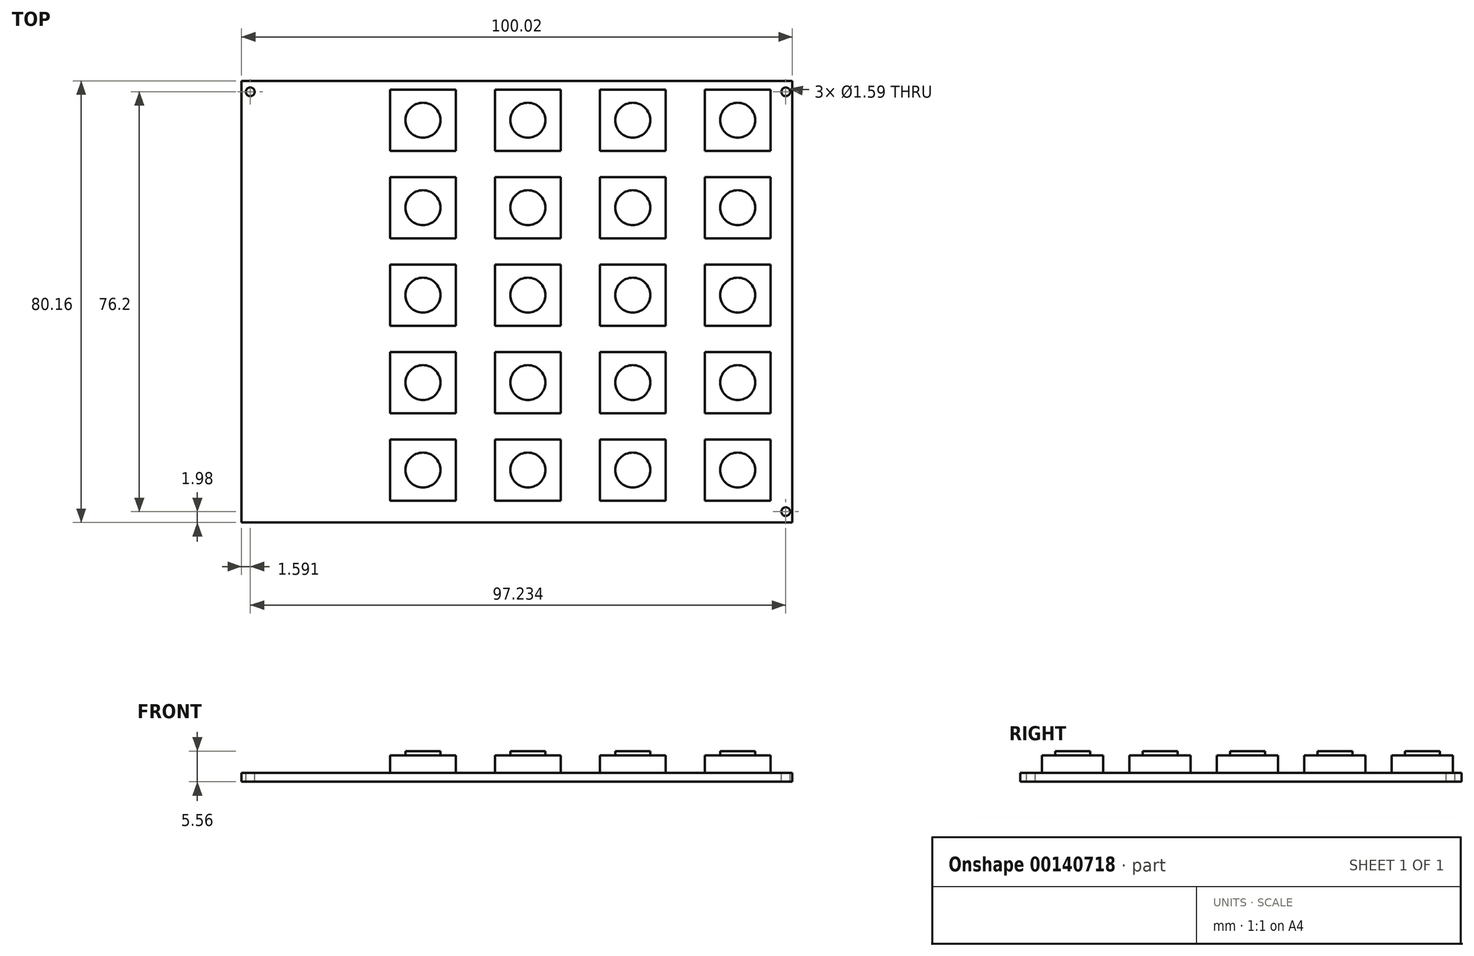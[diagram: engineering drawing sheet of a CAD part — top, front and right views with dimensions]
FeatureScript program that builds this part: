
annotation { "Feature Type Name" : "Feature", "Feature Type Description" : "" }
export const myFeature = defineFeature(function(context is Context, id is Id, definition is map)
    precondition{}
    {
        {
            var Q0;
            Q0=qCreatedBy(makeId("Top.planeOp"),FACE);
            var sketch = newSketch(context, id + "F0", { "sketchPlane" : qUnion([Q0])});
            skLineSegment(sketch, "E0.bottom", {"start": v(50, -40.08) * mm, "end": v(-50, -40.08) * mm});
            skLineSegment(sketch, "E0.top", {"start": v(50, 40.08) * mm, "end": v(-50, 40.08) * mm});
            skLineSegment(sketch, "E0.left", {"start": v(50, -40.08) * mm, "end": v(50, 40.08) * mm});
            skLineSegment(sketch, "E0.right", {"start": v(-50, -40.08) * mm, "end": v(-50, 40.08) * mm});
            skPoint(sketch, "E0.middle", {"position": v(0, 0) * mm});
            skSolve(sketch);
        }
        {
            var Q0;
            Q0 = qSketchRegion(id + "F0", true);
            extrude(context, id + "F1", {"entities" : qUnion([Q0]), "depth" : 1.59 * mm});
        }
        {
            var Q0;
            Q0=makeQuery(id+"F1.opExtrude","CAP_FACE",FACE,{"disambiguationData":[OSD([sQuery(id+"F0.wireOp",EDGE,"E0.bottom"),sQuery(id+"F0.wireOp",EDGE,"E0.top"),sQuery(id+"F0.wireOp",EDGE,"E0.left"),sQuery(id+"F0.wireOp",EDGE,"E0.right")])],"isStart":false});
            var sketch = newSketch(context, id + "F2", { "sketchPlane" : qUnion([Q0])});
            skLineSegment(sketch, "E1.0.0", {"start": v(-50, -40.08) * mm, "end": v(50, -40.08) * mm});
            skLineSegment(sketch, "E1.0.1", {"start": v(50, -40.08) * mm, "end": v(50, 40.08) * mm});
            skLineSegment(sketch, "E1.0.2", {"start": v(50, 40.08) * mm, "end": v(-50, 40.08) * mm});
            skLineSegment(sketch, "E1.0.3", {"start": v(-50, 40.08) * mm, "end": v(-50, -40.08) * mm});
            skLineSegment(sketch, "E2.bottom", {"start": v(50, -40.08) * mm, "end": v(46.04, -40.08) * mm});
            skLineSegment(sketch, "E2.top", {"start": v(50, -36.12) * mm, "end": v(46.04, -36.12) * mm});
            skLineSegment(sketch, "E2.left", {"start": v(50, -40.08) * mm, "end": v(50, -36.12) * mm});
            skLineSegment(sketch, "E2.right", {"start": v(46.04, -40.08) * mm, "end": v(46.04, -36.12) * mm});
            skLineSegment(sketch, "E3.bottom", {"start": v(46.04, -36.12) * mm, "end": v(34.13, -36.12) * mm});
            skLineSegment(sketch, "E3.top", {"start": v(46.04, -25) * mm, "end": v(34.13, -25) * mm});
            skLineSegment(sketch, "E3.left", {"start": v(46.04, -36.12) * mm, "end": v(46.04, -25) * mm});
            skLineSegment(sketch, "E3.right", {"start": v(34.13, -36.12) * mm, "end": v(34.13, -25) * mm});
            skLineSegment(sketch, "E4", {"start": v(40.08, 40.08) * mm, "end": v(40.08, 38.5) * mm});
            skLineSegment(sketch, "E5", {"start": v(-50, -30.15) * mm, "end": v(-23.02, -30.15) * mm});
            skLineSegment(sketch, "E6.0.1.0", {"start": v(46.04, -9.13) * mm, "end": v(34.13, -9.13) * mm});
            skLineSegment(sketch, "E6.0.1.1", {"start": v(34.13, -20.24) * mm, "end": v(34.13, -9.13) * mm});
            skLineSegment(sketch, "E6.0.1.2", {"start": v(46.04, -20.24) * mm, "end": v(34.13, -20.24) * mm});
            skLineSegment(sketch, "E6.0.1.3", {"start": v(46.04, -20.24) * mm, "end": v(46.04, -9.13) * mm});
            skLineSegment(sketch, "E6.0.2.0", {"start": v(46.04, 6.75) * mm, "end": v(34.13, 6.75) * mm});
            skLineSegment(sketch, "E6.0.2.1", {"start": v(34.13, -4.37) * mm, "end": v(34.13, 6.75) * mm});
            skLineSegment(sketch, "E6.0.2.2", {"start": v(46.04, -4.37) * mm, "end": v(34.13, -4.37) * mm});
            skLineSegment(sketch, "E6.0.2.3", {"start": v(46.04, -4.37) * mm, "end": v(46.04, 6.75) * mm});
            skLineSegment(sketch, "E6.0.3.0", {"start": v(46.04, 22.62) * mm, "end": v(34.13, 22.62) * mm});
            skLineSegment(sketch, "E6.0.3.1", {"start": v(34.13, 11.5) * mm, "end": v(34.13, 22.62) * mm});
            skLineSegment(sketch, "E6.0.3.2", {"start": v(46.04, 11.5) * mm, "end": v(34.13, 11.5) * mm});
            skLineSegment(sketch, "E6.0.3.3", {"start": v(46.04, 11.5) * mm, "end": v(46.04, 22.62) * mm});
            skLineSegment(sketch, "E6.0.4.0", {"start": v(46.04, 38.5) * mm, "end": v(34.13, 38.5) * mm});
            skLineSegment(sketch, "E6.0.4.1", {"start": v(34.13, 27.38) * mm, "end": v(34.13, 38.5) * mm});
            skLineSegment(sketch, "E6.0.4.2", {"start": v(46.04, 27.38) * mm, "end": v(34.13, 27.38) * mm});
            skLineSegment(sketch, "E6.0.4.3", {"start": v(46.04, 27.38) * mm, "end": v(46.04, 38.5) * mm});
            skLineSegment(sketch, "E6.1.0.0", {"start": v(26.99, -25) * mm, "end": v(15.08, -25) * mm});
            skLineSegment(sketch, "E6.1.0.1", {"start": v(15.08, -36.12) * mm, "end": v(15.08, -25) * mm});
            skLineSegment(sketch, "E6.1.0.2", {"start": v(26.99, -36.12) * mm, "end": v(15.08, -36.12) * mm});
            skLineSegment(sketch, "E6.1.0.3", {"start": v(26.99, -36.12) * mm, "end": v(26.99, -25) * mm});
            skLineSegment(sketch, "E6.1.1.0", {"start": v(26.99, -9.13) * mm, "end": v(15.08, -9.13) * mm});
            skLineSegment(sketch, "E6.1.1.1", {"start": v(15.08, -20.24) * mm, "end": v(15.08, -9.13) * mm});
            skLineSegment(sketch, "E6.1.1.2", {"start": v(26.99, -20.24) * mm, "end": v(15.08, -20.24) * mm});
            skLineSegment(sketch, "E6.1.1.3", {"start": v(26.99, -20.24) * mm, "end": v(26.99, -9.13) * mm});
            skLineSegment(sketch, "E6.1.2.0", {"start": v(26.99, 6.75) * mm, "end": v(15.08, 6.75) * mm});
            skLineSegment(sketch, "E6.1.2.1", {"start": v(15.08, -4.37) * mm, "end": v(15.08, 6.75) * mm});
            skLineSegment(sketch, "E6.1.2.2", {"start": v(26.99, -4.37) * mm, "end": v(15.08, -4.37) * mm});
            skLineSegment(sketch, "E6.1.2.3", {"start": v(26.99, -4.37) * mm, "end": v(26.99, 6.75) * mm});
            skLineSegment(sketch, "E6.1.3.0", {"start": v(26.99, 22.62) * mm, "end": v(15.08, 22.62) * mm});
            skLineSegment(sketch, "E6.1.3.1", {"start": v(15.08, 11.5) * mm, "end": v(15.08, 22.62) * mm});
            skLineSegment(sketch, "E6.1.3.2", {"start": v(26.99, 11.5) * mm, "end": v(15.08, 11.5) * mm});
            skLineSegment(sketch, "E6.1.3.3", {"start": v(26.99, 11.5) * mm, "end": v(26.99, 22.62) * mm});
            skLineSegment(sketch, "E6.1.4.0", {"start": v(26.99, 38.5) * mm, "end": v(15.08, 38.5) * mm});
            skLineSegment(sketch, "E6.1.4.1", {"start": v(15.08, 27.38) * mm, "end": v(15.08, 38.5) * mm});
            skLineSegment(sketch, "E6.1.4.2", {"start": v(26.99, 27.38) * mm, "end": v(15.08, 27.38) * mm});
            skLineSegment(sketch, "E6.1.4.3", {"start": v(26.99, 27.38) * mm, "end": v(26.99, 38.5) * mm});
            skLineSegment(sketch, "E6.2.0.0", {"start": v(7.94, -25) * mm, "end": v(-3.97, -25) * mm});
            skLineSegment(sketch, "E6.2.0.1", {"start": v(-3.97, -36.12) * mm, "end": v(-3.97, -25) * mm});
            skLineSegment(sketch, "E6.2.0.2", {"start": v(7.94, -36.12) * mm, "end": v(-3.97, -36.12) * mm});
            skLineSegment(sketch, "E6.2.0.3", {"start": v(7.94, -36.12) * mm, "end": v(7.94, -25) * mm});
            skLineSegment(sketch, "E6.2.1.0", {"start": v(7.94, -9.13) * mm, "end": v(-3.97, -9.13) * mm});
            skLineSegment(sketch, "E6.2.1.1", {"start": v(-3.97, -20.24) * mm, "end": v(-3.97, -9.13) * mm});
            skLineSegment(sketch, "E6.2.1.2", {"start": v(7.94, -20.24) * mm, "end": v(-3.97, -20.24) * mm});
            skLineSegment(sketch, "E6.2.1.3", {"start": v(7.94, -20.24) * mm, "end": v(7.94, -9.13) * mm});
            skLineSegment(sketch, "E6.2.2.0", {"start": v(7.94, 6.75) * mm, "end": v(-3.97, 6.75) * mm});
            skLineSegment(sketch, "E6.2.2.1", {"start": v(-3.97, -4.37) * mm, "end": v(-3.97, 6.75) * mm});
            skLineSegment(sketch, "E6.2.2.2", {"start": v(7.94, -4.37) * mm, "end": v(-3.97, -4.37) * mm});
            skLineSegment(sketch, "E6.2.2.3", {"start": v(7.94, -4.37) * mm, "end": v(7.94, 6.75) * mm});
            skLineSegment(sketch, "E6.2.3.0", {"start": v(7.94, 22.62) * mm, "end": v(-3.97, 22.62) * mm});
            skLineSegment(sketch, "E6.2.3.1", {"start": v(-3.97, 11.5) * mm, "end": v(-3.97, 22.62) * mm});
            skLineSegment(sketch, "E6.2.3.2", {"start": v(7.94, 11.5) * mm, "end": v(-3.97, 11.5) * mm});
            skLineSegment(sketch, "E6.2.3.3", {"start": v(7.94, 11.5) * mm, "end": v(7.94, 22.62) * mm});
            skLineSegment(sketch, "E6.2.4.0", {"start": v(7.94, 38.5) * mm, "end": v(-3.97, 38.5) * mm});
            skLineSegment(sketch, "E6.2.4.1", {"start": v(-3.97, 27.38) * mm, "end": v(-3.97, 38.5) * mm});
            skLineSegment(sketch, "E6.2.4.2", {"start": v(7.94, 27.38) * mm, "end": v(-3.97, 27.38) * mm});
            skLineSegment(sketch, "E6.2.4.3", {"start": v(7.94, 27.38) * mm, "end": v(7.94, 38.5) * mm});
            skLineSegment(sketch, "E6.3.0.0", {"start": v(-11.11, -25) * mm, "end": v(-23.02, -25) * mm});
            skLineSegment(sketch, "E6.3.0.1", {"start": v(-23.02, -36.12) * mm, "end": v(-23.02, -25) * mm});
            skLineSegment(sketch, "E6.3.0.2", {"start": v(-11.11, -36.12) * mm, "end": v(-23.02, -36.12) * mm});
            skLineSegment(sketch, "E6.3.0.3", {"start": v(-11.11, -36.12) * mm, "end": v(-11.11, -25) * mm});
            skLineSegment(sketch, "E6.3.1.0", {"start": v(-11.11, -9.13) * mm, "end": v(-23.02, -9.13) * mm});
            skLineSegment(sketch, "E6.3.1.1", {"start": v(-23.02, -20.24) * mm, "end": v(-23.02, -9.13) * mm});
            skLineSegment(sketch, "E6.3.1.2", {"start": v(-11.11, -20.24) * mm, "end": v(-23.02, -20.24) * mm});
            skLineSegment(sketch, "E6.3.1.3", {"start": v(-11.11, -20.24) * mm, "end": v(-11.11, -9.13) * mm});
            skLineSegment(sketch, "E6.3.2.0", {"start": v(-11.11, 6.75) * mm, "end": v(-23.02, 6.75) * mm});
            skLineSegment(sketch, "E6.3.2.1", {"start": v(-23.02, -4.37) * mm, "end": v(-23.02, 6.75) * mm});
            skLineSegment(sketch, "E6.3.2.2", {"start": v(-11.11, -4.37) * mm, "end": v(-23.02, -4.37) * mm});
            skLineSegment(sketch, "E6.3.2.3", {"start": v(-11.11, -4.37) * mm, "end": v(-11.11, 6.75) * mm});
            skLineSegment(sketch, "E6.3.3.0", {"start": v(-11.11, 22.62) * mm, "end": v(-23.02, 22.62) * mm});
            skLineSegment(sketch, "E6.3.3.1", {"start": v(-23.02, 11.5) * mm, "end": v(-23.02, 22.62) * mm});
            skLineSegment(sketch, "E6.3.3.2", {"start": v(-11.11, 11.5) * mm, "end": v(-23.02, 11.5) * mm});
            skLineSegment(sketch, "E6.3.3.3", {"start": v(-11.11, 11.5) * mm, "end": v(-11.11, 22.62) * mm});
            skLineSegment(sketch, "E6.3.4.0", {"start": v(-11.11, 38.5) * mm, "end": v(-23.02, 38.5) * mm});
            skLineSegment(sketch, "E6.3.4.1", {"start": v(-23.02, 27.38) * mm, "end": v(-23.02, 38.5) * mm});
            skLineSegment(sketch, "E6.3.4.2", {"start": v(-11.11, 27.38) * mm, "end": v(-23.02, 27.38) * mm});
            skLineSegment(sketch, "E6.3.4.3", {"start": v(-11.11, 27.38) * mm, "end": v(-11.11, 38.5) * mm});
            skLineSegment(sketch, "E6.direction1", {"start": v(34.13, -25) * mm, "end": v(15.08, -25) * mm, "construction": true});
            skLineSegment(sketch, "E6.direction2", {"start": v(34.13, -25) * mm, "end": v(34.13, -9.13) * mm, "construction": true});
            skSolve(sketch);
        }
        {
            var Q0;
            Q0=makeQuery(id+"F2.imprint","IMPRINT",FACE,{"disambiguationData":[TD([[makeQuery(id+"F2.imprint","IMPRINT",EDGE,{"derivedFrom":sQuery(id+"F2.wireOp",EDGE,"E6.3.4.0")}),1.0]])]});
            var Q1;
            Q1=makeQuery(id+"F2.imprint","IMPRINT",FACE,{"disambiguationData":[TD([[makeQuery(id+"F2.imprint","IMPRINT",EDGE,{"derivedFrom":sQuery(id+"F2.wireOp",EDGE,"E6.2.4.0")}),1.0]])]});
            var Q2;
            Q2=makeQuery(id+"F2.imprint","IMPRINT",FACE,{"disambiguationData":[TD([[makeQuery(id+"F2.imprint","IMPRINT",EDGE,{"derivedFrom":sQuery(id+"F2.wireOp",EDGE,"E6.1.4.0")}),1.0]])]});
            var Q3;
            {var subQ0=sQuery(id+"F2.wireOp",EDGE,"E6.0.4.1");Q3=makeQuery(id+"F2.imprint","IMPRINT",FACE,{"disambiguationData":[TD([[makeQuery(id+"F2.imprint","IMPRINT",EDGE,{"derivedFrom":subQ0}),-1.0]])]});}
            var Q4;
            Q4=makeQuery(id+"F2.imprint","IMPRINT",FACE,{"disambiguationData":[TD([[makeQuery(id+"F2.imprint","IMPRINT",EDGE,{"derivedFrom":sQuery(id+"F2.wireOp",EDGE,"E6.0.3.0")}),1.0]])]});
            var Q5;
            Q5=makeQuery(id+"F2.imprint","IMPRINT",FACE,{"disambiguationData":[TD([[makeQuery(id+"F2.imprint","IMPRINT",EDGE,{"derivedFrom":sQuery(id+"F2.wireOp",EDGE,"E6.0.2.0")}),1.0]])]});
            var Q6;
            Q6=makeQuery(id+"F2.imprint","IMPRINT",FACE,{"disambiguationData":[TD([[makeQuery(id+"F2.imprint","IMPRINT",EDGE,{"derivedFrom":sQuery(id+"F2.wireOp",EDGE,"E6.0.1.0")}),1.0]])]});
            var Q7;
            Q7=makeQuery(id+"F2.imprint","IMPRINT",FACE,{"disambiguationData":[TD([[makeQuery(id+"F2.imprint","IMPRINT",EDGE,{"derivedFrom":sQuery(id+"F2.wireOp",EDGE,"E3.bottom")}),-1.0]])]});
            var Q8;
            Q8=makeQuery(id+"F2.imprint","IMPRINT",FACE,{"disambiguationData":[TD([[makeQuery(id+"F2.imprint","IMPRINT",EDGE,{"derivedFrom":sQuery(id+"F2.wireOp",EDGE,"E6.1.0.0")}),1.0]])]});
            var Q9;
            Q9=makeQuery(id+"F2.imprint","IMPRINT",FACE,{"disambiguationData":[TD([[makeQuery(id+"F2.imprint","IMPRINT",EDGE,{"derivedFrom":sQuery(id+"F2.wireOp",EDGE,"E6.2.0.0")}),1.0]])]});
            var Q10;
            {var subQ3=sQuery(id+"F2.wireOp",EDGE,"E6.3.0.0");Q10=makeQuery(id+"F2.imprint","IMPRINT",FACE,{"disambiguationData":[TD([[makeQuery(id+"F2.imprint","IMPRINT",EDGE,{"derivedFrom":subQ3}),1.0]])]});}
            var Q11;
            Q11=makeQuery(id+"F2.imprint","IMPRINT",FACE,{"disambiguationData":[TD([[makeQuery(id+"F2.imprint","IMPRINT",EDGE,{"derivedFrom":sQuery(id+"F2.wireOp",EDGE,"E6.3.1.0")}),1.0]])]});
            var Q12;
            Q12=makeQuery(id+"F2.imprint","IMPRINT",FACE,{"disambiguationData":[TD([[makeQuery(id+"F2.imprint","IMPRINT",EDGE,{"derivedFrom":sQuery(id+"F2.wireOp",EDGE,"E6.3.2.0")}),1.0]])]});
            var Q13;
            Q13=makeQuery(id+"F2.imprint","IMPRINT",FACE,{"disambiguationData":[TD([[makeQuery(id+"F2.imprint","IMPRINT",EDGE,{"derivedFrom":sQuery(id+"F2.wireOp",EDGE,"E6.3.3.0")}),1.0]])]});
            var Q14;
            Q14=makeQuery(id+"F2.imprint","IMPRINT",FACE,{"disambiguationData":[TD([[makeQuery(id+"F2.imprint","IMPRINT",EDGE,{"derivedFrom":sQuery(id+"F2.wireOp",EDGE,"E6.2.3.0")}),1.0]])]});
            var Q15;
            Q15=makeQuery(id+"F2.imprint","IMPRINT",FACE,{"disambiguationData":[TD([[makeQuery(id+"F2.imprint","IMPRINT",EDGE,{"derivedFrom":sQuery(id+"F2.wireOp",EDGE,"E6.1.3.0")}),1.0]])]});
            var Q16;
            Q16=makeQuery(id+"F2.imprint","IMPRINT",FACE,{"disambiguationData":[TD([[makeQuery(id+"F2.imprint","IMPRINT",EDGE,{"derivedFrom":sQuery(id+"F2.wireOp",EDGE,"E6.1.2.0")}),1.0]])]});
            var Q17;
            Q17=makeQuery(id+"F2.imprint","IMPRINT",FACE,{"disambiguationData":[TD([[makeQuery(id+"F2.imprint","IMPRINT",EDGE,{"derivedFrom":sQuery(id+"F2.wireOp",EDGE,"E6.2.2.0")}),1.0]])]});
            var Q18;
            Q18=makeQuery(id+"F2.imprint","IMPRINT",FACE,{"disambiguationData":[TD([[makeQuery(id+"F2.imprint","IMPRINT",EDGE,{"derivedFrom":sQuery(id+"F2.wireOp",EDGE,"E6.2.1.0")}),1.0]])]});
            var Q19;
            Q19=makeQuery(id+"F2.imprint","IMPRINT",FACE,{"disambiguationData":[TD([[makeQuery(id+"F2.imprint","IMPRINT",EDGE,{"derivedFrom":sQuery(id+"F2.wireOp",EDGE,"E6.1.1.0")}),1.0]])]});
            extrude(context, id + "F3", {"entities" : qUnion([Q0, Q1, Q2, Q3, Q4, Q5, Q6, Q7, Q8, Q9, Q10, Q11, Q12, Q13, Q14, Q15, Q16, Q17, Q18, Q19]), "operationType" : NewBodyOperationType.ADD, "depth" : 3.17 * mm});
        }
        {
            var Q0;
            Q0=makeQuery(id+"F3.opExtrude","CAP_FACE",FACE,{"disambiguationData":[OSD([sQuery(id+"F2.wireOp",EDGE,"E6.2.3.0"),sQuery(id+"F2.wireOp",EDGE,"E6.2.3.1"),sQuery(id+"F2.wireOp",EDGE,"E6.2.3.2"),sQuery(id+"F2.wireOp",EDGE,"E6.2.3.3")])],"isStart":false});
            var sketch = newSketch(context, id + "F4", { "sketchPlane" : qUnion([Q0])});
            skLineSegment(sketch, "E7.0.0", {"start": v(-11.11, 27.38) * mm, "end": v(-11.11, 38.5) * mm});
            skLineSegment(sketch, "E7.0.1", {"start": v(-11.11, 38.5) * mm, "end": v(-23.02, 38.5) * mm});
            skLineSegment(sketch, "E7.0.2", {"start": v(-23.02, 38.5) * mm, "end": v(-23.02, 27.38) * mm});
            skLineSegment(sketch, "E7.0.3", {"start": v(-23.02, 27.38) * mm, "end": v(-11.11, 27.38) * mm});
            skLineSegment(sketch, "E8.0.0", {"start": v(7.94, 27.38) * mm, "end": v(7.94, 38.5) * mm});
            skLineSegment(sketch, "E8.0.1", {"start": v(7.94, 38.5) * mm, "end": v(-3.97, 38.5) * mm});
            skLineSegment(sketch, "E8.0.2", {"start": v(-3.97, 38.5) * mm, "end": v(-3.97, 27.38) * mm});
            skLineSegment(sketch, "E8.0.3", {"start": v(-3.97, 27.38) * mm, "end": v(7.94, 27.38) * mm});
            skLineSegment(sketch, "E9.0.0", {"start": v(26.99, 27.38) * mm, "end": v(26.99, 38.5) * mm});
            skLineSegment(sketch, "E9.0.1", {"start": v(26.99, 38.5) * mm, "end": v(15.08, 38.5) * mm});
            skLineSegment(sketch, "E9.0.2", {"start": v(15.08, 38.5) * mm, "end": v(15.08, 27.38) * mm});
            skLineSegment(sketch, "E9.0.3", {"start": v(15.08, 27.38) * mm, "end": v(26.99, 27.38) * mm});
            skLineSegment(sketch, "E10.0.0", {"start": v(46.04, 27.38) * mm, "end": v(46.04, 38.5) * mm});
            skLineSegment(sketch, "E10.0.1", {"start": v(46.04, 38.5) * mm, "end": v(34.13, 38.5) * mm});
            skLineSegment(sketch, "E10.0.2", {"start": v(34.13, 38.5) * mm, "end": v(34.13, 27.38) * mm});
            skLineSegment(sketch, "E10.0.3", {"start": v(34.13, 27.38) * mm, "end": v(46.04, 27.38) * mm});
            skLineSegment(sketch, "E11.0.0", {"start": v(46.04, 11.5) * mm, "end": v(46.04, 22.62) * mm});
            skLineSegment(sketch, "E11.0.1", {"start": v(46.04, 22.62) * mm, "end": v(34.13, 22.62) * mm});
            skLineSegment(sketch, "E11.0.2", {"start": v(34.13, 22.62) * mm, "end": v(34.13, 11.5) * mm});
            skLineSegment(sketch, "E11.0.3", {"start": v(34.13, 11.5) * mm, "end": v(46.04, 11.5) * mm});
            skLineSegment(sketch, "E12.0.0", {"start": v(46.04, -4.37) * mm, "end": v(46.04, 6.75) * mm});
            skLineSegment(sketch, "E12.0.1", {"start": v(46.04, 6.75) * mm, "end": v(34.13, 6.75) * mm});
            skLineSegment(sketch, "E12.0.2", {"start": v(34.13, 6.75) * mm, "end": v(34.13, -4.37) * mm});
            skLineSegment(sketch, "E12.0.3", {"start": v(34.13, -4.37) * mm, "end": v(46.04, -4.37) * mm});
            skLineSegment(sketch, "E13.0.0", {"start": v(46.04, -20.24) * mm, "end": v(46.04, -9.13) * mm});
            skLineSegment(sketch, "E13.0.1", {"start": v(46.04, -9.13) * mm, "end": v(34.13, -9.13) * mm});
            skLineSegment(sketch, "E13.0.2", {"start": v(34.13, -9.13) * mm, "end": v(34.13, -20.24) * mm});
            skLineSegment(sketch, "E13.0.3", {"start": v(34.13, -20.24) * mm, "end": v(46.04, -20.24) * mm});
            skLineSegment(sketch, "E14.0.0", {"start": v(34.13, -36.12) * mm, "end": v(46.04, -36.12) * mm});
            skLineSegment(sketch, "E14.0.1", {"start": v(46.04, -36.12) * mm, "end": v(46.04, -25) * mm});
            skLineSegment(sketch, "E14.0.2", {"start": v(46.04, -25) * mm, "end": v(34.13, -25) * mm});
            skLineSegment(sketch, "E14.0.3", {"start": v(34.13, -25) * mm, "end": v(34.13, -36.12) * mm});
            skLineSegment(sketch, "E15.0.0", {"start": v(26.99, -36.12) * mm, "end": v(26.99, -25) * mm});
            skLineSegment(sketch, "E15.0.1", {"start": v(26.99, -25) * mm, "end": v(15.08, -25) * mm});
            skLineSegment(sketch, "E15.0.2", {"start": v(15.08, -25) * mm, "end": v(15.08, -36.12) * mm});
            skLineSegment(sketch, "E15.0.3", {"start": v(15.08, -36.12) * mm, "end": v(26.99, -36.12) * mm});
            skLineSegment(sketch, "E16.0.0", {"start": v(7.94, -36.12) * mm, "end": v(7.94, -25) * mm});
            skLineSegment(sketch, "E16.0.1", {"start": v(7.94, -25) * mm, "end": v(-3.97, -25) * mm});
            skLineSegment(sketch, "E16.0.2", {"start": v(-3.97, -25) * mm, "end": v(-3.97, -36.12) * mm});
            skLineSegment(sketch, "E16.0.3", {"start": v(-3.97, -36.12) * mm, "end": v(7.94, -36.12) * mm});
            skLineSegment(sketch, "E17.0.0", {"start": v(-11.11, -36.12) * mm, "end": v(-11.11, -25) * mm});
            skLineSegment(sketch, "E17.0.1", {"start": v(-11.11, -25) * mm, "end": v(-23.02, -25) * mm});
            skLineSegment(sketch, "E17.0.2", {"start": v(-23.02, -25) * mm, "end": v(-23.02, -36.12) * mm});
            skLineSegment(sketch, "E17.0.3", {"start": v(-23.02, -36.12) * mm, "end": v(-11.11, -36.12) * mm});
            skLineSegment(sketch, "E18.0.0", {"start": v(-11.11, -20.24) * mm, "end": v(-11.11, -9.13) * mm});
            skLineSegment(sketch, "E18.0.1", {"start": v(-11.11, -9.13) * mm, "end": v(-23.02, -9.13) * mm});
            skLineSegment(sketch, "E18.0.2", {"start": v(-23.02, -9.13) * mm, "end": v(-23.02, -20.24) * mm});
            skLineSegment(sketch, "E18.0.3", {"start": v(-23.02, -20.24) * mm, "end": v(-11.11, -20.24) * mm});
            skLineSegment(sketch, "E19.0.0", {"start": v(-11.11, -4.37) * mm, "end": v(-11.11, 6.75) * mm});
            skLineSegment(sketch, "E19.0.1", {"start": v(-11.11, 6.75) * mm, "end": v(-23.02, 6.75) * mm});
            skLineSegment(sketch, "E19.0.2", {"start": v(-23.02, 6.75) * mm, "end": v(-23.02, -4.37) * mm});
            skLineSegment(sketch, "E19.0.3", {"start": v(-23.02, -4.37) * mm, "end": v(-11.11, -4.37) * mm});
            skLineSegment(sketch, "E20.0.0", {"start": v(-11.11, 11.5) * mm, "end": v(-11.11, 22.62) * mm});
            skLineSegment(sketch, "E20.0.1", {"start": v(-11.11, 22.62) * mm, "end": v(-23.02, 22.62) * mm});
            skLineSegment(sketch, "E20.0.2", {"start": v(-23.02, 22.62) * mm, "end": v(-23.02, 11.5) * mm});
            skLineSegment(sketch, "E20.0.3", {"start": v(-23.02, 11.5) * mm, "end": v(-11.11, 11.5) * mm});
            skLineSegment(sketch, "E21.0.0", {"start": v(7.94, 11.5) * mm, "end": v(7.94, 22.62) * mm});
            skLineSegment(sketch, "E21.0.1", {"start": v(7.94, 22.62) * mm, "end": v(-3.97, 22.62) * mm});
            skLineSegment(sketch, "E21.0.2", {"start": v(-3.97, 22.62) * mm, "end": v(-3.97, 11.5) * mm});
            skLineSegment(sketch, "E21.0.3", {"start": v(-3.97, 11.5) * mm, "end": v(7.94, 11.5) * mm});
            skLineSegment(sketch, "E22.0.0", {"start": v(7.94, -4.37) * mm, "end": v(7.94, 6.75) * mm});
            skLineSegment(sketch, "E22.0.1", {"start": v(7.94, 6.75) * mm, "end": v(-3.97, 6.75) * mm});
            skLineSegment(sketch, "E22.0.2", {"start": v(-3.97, 6.75) * mm, "end": v(-3.97, -4.37) * mm});
            skLineSegment(sketch, "E22.0.3", {"start": v(-3.97, -4.37) * mm, "end": v(7.94, -4.37) * mm});
            skLineSegment(sketch, "E23.0", {"start": v(7.94, -20.24) * mm, "end": v(-3.97, -20.24) * mm});
            skLineSegment(sketch, "E24.0.0", {"start": v(26.99, -20.24) * mm, "end": v(26.99, -9.13) * mm});
            skLineSegment(sketch, "E24.0.1", {"start": v(26.99, -9.13) * mm, "end": v(15.08, -9.13) * mm});
            skLineSegment(sketch, "E24.0.2", {"start": v(15.08, -9.13) * mm, "end": v(15.08, -20.24) * mm});
            skLineSegment(sketch, "E24.0.3", {"start": v(15.08, -20.24) * mm, "end": v(26.99, -20.24) * mm});
            skLineSegment(sketch, "E25.0.0", {"start": v(26.99, -4.37) * mm, "end": v(26.99, 6.75) * mm});
            skLineSegment(sketch, "E25.0.1", {"start": v(26.99, 6.75) * mm, "end": v(15.08, 6.75) * mm});
            skLineSegment(sketch, "E25.0.2", {"start": v(15.08, 6.75) * mm, "end": v(15.08, -4.37) * mm});
            skLineSegment(sketch, "E25.0.3", {"start": v(15.08, -4.37) * mm, "end": v(26.99, -4.37) * mm});
            skLineSegment(sketch, "E26.0.0", {"start": v(26.99, 11.5) * mm, "end": v(26.99, 22.62) * mm});
            skLineSegment(sketch, "E26.0.1", {"start": v(26.99, 22.62) * mm, "end": v(15.08, 22.62) * mm});
            skLineSegment(sketch, "E26.0.2", {"start": v(15.08, 22.62) * mm, "end": v(15.08, 11.5) * mm});
            skLineSegment(sketch, "E26.0.3", {"start": v(15.08, 11.5) * mm, "end": v(26.99, 11.5) * mm});
            skLineSegment(sketch, "E27.0.0", {"start": v(7.94, -20.24) * mm, "end": v(7.94, -9.13) * mm});
            skLineSegment(sketch, "E27.0.1", {"start": v(7.94, -9.13) * mm, "end": v(-3.97, -9.13) * mm});
            skLineSegment(sketch, "E27.0.2", {"start": v(-3.97, -9.13) * mm, "end": v(-3.97, -20.24) * mm});
            skLineSegment(sketch, "E27.0.3", {"start": v(-3.97, -20.24) * mm, "end": v(7.94, -20.24) * mm});
            skCircle(sketch, "E28", {"center": v(40.08, -30.56) * mm, "radius": 3.18 * mm});
            skCircle(sketch, "E29.0.1.0", {"center": v(40.08, -14.68) * mm, "radius": 3.18 * mm});
            skCircle(sketch, "E29.0.2.0", {"center": v(40.08, 1.2) * mm, "radius": 3.18 * mm});
            skCircle(sketch, "E29.0.3.0", {"center": v(40.08, 17.07) * mm, "radius": 3.18 * mm});
            skCircle(sketch, "E29.0.4.0", {"center": v(40.08, 32.94) * mm, "radius": 3.18 * mm});
            skCircle(sketch, "E29.1.0.0", {"center": v(21.03, -30.56) * mm, "radius": 3.18 * mm});
            skCircle(sketch, "E29.1.1.0", {"center": v(21.03, -14.68) * mm, "radius": 3.18 * mm});
            skCircle(sketch, "E29.1.2.0", {"center": v(21.03, 1.2) * mm, "radius": 3.18 * mm});
            skCircle(sketch, "E29.1.3.0", {"center": v(21.03, 17.07) * mm, "radius": 3.18 * mm});
            skCircle(sketch, "E29.1.4.0", {"center": v(21.03, 32.94) * mm, "radius": 3.18 * mm});
            skCircle(sketch, "E29.2.0.0", {"center": v(1.98, -30.56) * mm, "radius": 3.18 * mm});
            skCircle(sketch, "E29.2.1.0", {"center": v(1.98, -14.68) * mm, "radius": 3.18 * mm});
            skCircle(sketch, "E29.2.2.0", {"center": v(1.98, 1.2) * mm, "radius": 3.18 * mm});
            skCircle(sketch, "E29.2.3.0", {"center": v(1.98, 17.07) * mm, "radius": 3.18 * mm});
            skCircle(sketch, "E29.2.4.0", {"center": v(1.98, 32.94) * mm, "radius": 3.18 * mm});
            skCircle(sketch, "E29.3.0.0", {"center": v(-17.07, -30.56) * mm, "radius": 3.18 * mm});
            skLineSegment(sketch, "E29.3.0.1", {"start": v(-42.07, -36.12) * mm, "end": v(-30.16, -36.12) * mm});
            skCircle(sketch, "E29.3.1.0", {"center": v(-17.07, -14.68) * mm, "radius": 3.18 * mm});
            skLineSegment(sketch, "E29.3.1.1", {"start": v(-42.07, -20.24) * mm, "end": v(-30.16, -20.24) * mm});
            skCircle(sketch, "E29.3.2.0", {"center": v(-17.07, 1.2) * mm, "radius": 3.18 * mm});
            skLineSegment(sketch, "E29.3.2.1", {"start": v(-42.07, -4.37) * mm, "end": v(-30.16, -4.37) * mm});
            skCircle(sketch, "E29.3.3.0", {"center": v(-17.07, 17.07) * mm, "radius": 3.18 * mm});
            skLineSegment(sketch, "E29.3.3.1", {"start": v(-42.07, 11.5) * mm, "end": v(-30.16, 11.5) * mm});
            skCircle(sketch, "E29.3.4.0", {"center": v(-17.07, 32.94) * mm, "radius": 3.18 * mm});
            skLineSegment(sketch, "E29.3.4.1", {"start": v(-42.07, 27.38) * mm, "end": v(-30.16, 27.38) * mm});
            skLineSegment(sketch, "E29.direction1", {"start": v(40.08, -30.56) * mm, "end": v(21.03, -30.56) * mm, "construction": true});
            skLineSegment(sketch, "E29.direction2", {"start": v(40.08, -30.56) * mm, "end": v(40.08, -14.68) * mm, "construction": true});
            skSolve(sketch);
        }
        {
            var Q0;
            Q0=makeQuery(id+"F4.imprint","IMPRINT",FACE,{"disambiguationData":[TD([[makeQuery(id+"F4.imprint","IMPRINT",EDGE,{"derivedFrom":sQuery(id+"F4.wireOp",EDGE,"E28")}),1.0]])]});
            var Q1;
            Q1=makeQuery(id+"F4.imprint","IMPRINT",FACE,{"disambiguationData":[TD([[makeQuery(id+"F4.imprint","IMPRINT",EDGE,{"derivedFrom":sQuery(id+"F4.wireOp",EDGE,"E29.0.1.0")}),1.0]])]});
            var Q2;
            Q2=makeQuery(id+"F4.imprint","IMPRINT",FACE,{"disambiguationData":[TD([[makeQuery(id+"F4.imprint","IMPRINT",EDGE,{"derivedFrom":sQuery(id+"F4.wireOp",EDGE,"E29.0.2.0")}),1.0]])]});
            var Q3;
            Q3=makeQuery(id+"F4.imprint","IMPRINT",FACE,{"disambiguationData":[TD([[makeQuery(id+"F4.imprint","IMPRINT",EDGE,{"derivedFrom":sQuery(id+"F4.wireOp",EDGE,"E29.0.3.0")}),1.0]])]});
            var Q4;
            Q4=makeQuery(id+"F4.imprint","IMPRINT",FACE,{"disambiguationData":[TD([[makeQuery(id+"F4.imprint","IMPRINT",EDGE,{"derivedFrom":sQuery(id+"F4.wireOp",EDGE,"E29.0.4.0")}),1.0]])]});
            var Q5;
            Q5=makeQuery(id+"F4.imprint","IMPRINT",FACE,{"disambiguationData":[TD([[makeQuery(id+"F4.imprint","IMPRINT",EDGE,{"derivedFrom":sQuery(id+"F4.wireOp",EDGE,"E29.1.4.0")}),1.0]])]});
            var Q6;
            Q6=makeQuery(id+"F4.imprint","IMPRINT",FACE,{"disambiguationData":[TD([[makeQuery(id+"F4.imprint","IMPRINT",EDGE,{"derivedFrom":sQuery(id+"F4.wireOp",EDGE,"E29.1.3.0")}),1.0]])]});
            var Q7;
            Q7=makeQuery(id+"F4.imprint","IMPRINT",FACE,{"disambiguationData":[TD([[makeQuery(id+"F4.imprint","IMPRINT",EDGE,{"derivedFrom":sQuery(id+"F4.wireOp",EDGE,"E29.1.2.0")}),1.0]])]});
            var Q8;
            Q8=makeQuery(id+"F4.imprint","IMPRINT",FACE,{"disambiguationData":[TD([[makeQuery(id+"F4.imprint","IMPRINT",EDGE,{"derivedFrom":sQuery(id+"F4.wireOp",EDGE,"E29.1.1.0")}),1.0]])]});
            var Q9;
            Q9=makeQuery(id+"F4.imprint","IMPRINT",FACE,{"disambiguationData":[TD([[makeQuery(id+"F4.imprint","IMPRINT",EDGE,{"derivedFrom":sQuery(id+"F4.wireOp",EDGE,"E29.1.0.0")}),1.0]])]});
            var Q10;
            Q10=makeQuery(id+"F4.imprint","IMPRINT",FACE,{"disambiguationData":[TD([[makeQuery(id+"F4.imprint","IMPRINT",EDGE,{"derivedFrom":sQuery(id+"F4.wireOp",EDGE,"E29.2.0.0")}),1.0]])]});
            var Q11;
            Q11=makeQuery(id+"F4.imprint","IMPRINT",FACE,{"disambiguationData":[TD([[makeQuery(id+"F4.imprint","IMPRINT",EDGE,{"derivedFrom":sQuery(id+"F4.wireOp",EDGE,"E29.2.1.0")}),1.0]])]});
            var Q12;
            Q12=makeQuery(id+"F4.imprint","IMPRINT",FACE,{"disambiguationData":[TD([[makeQuery(id+"F4.imprint","IMPRINT",EDGE,{"derivedFrom":sQuery(id+"F4.wireOp",EDGE,"E29.2.2.0")}),1.0]])]});
            var Q13;
            Q13=makeQuery(id+"F4.imprint","IMPRINT",FACE,{"disambiguationData":[TD([[makeQuery(id+"F4.imprint","IMPRINT",EDGE,{"derivedFrom":sQuery(id+"F4.wireOp",EDGE,"E29.2.3.0")}),1.0]])]});
            var Q14;
            Q14=makeQuery(id+"F4.imprint","IMPRINT",FACE,{"disambiguationData":[TD([[makeQuery(id+"F4.imprint","IMPRINT",EDGE,{"derivedFrom":sQuery(id+"F4.wireOp",EDGE,"E29.2.4.0")}),1.0]])]});
            var Q15;
            Q15=makeQuery(id+"F4.imprint","IMPRINT",FACE,{"disambiguationData":[TD([[makeQuery(id+"F4.imprint","IMPRINT",EDGE,{"derivedFrom":sQuery(id+"F4.wireOp",EDGE,"E29.3.4.0")}),1.0]])]});
            var Q16;
            Q16=makeQuery(id+"F4.imprint","IMPRINT",FACE,{"disambiguationData":[TD([[makeQuery(id+"F4.imprint","IMPRINT",EDGE,{"derivedFrom":sQuery(id+"F4.wireOp",EDGE,"E29.3.3.0")}),1.0]])]});
            var Q17;
            Q17=makeQuery(id+"F4.imprint","IMPRINT",FACE,{"disambiguationData":[TD([[makeQuery(id+"F4.imprint","IMPRINT",EDGE,{"derivedFrom":sQuery(id+"F4.wireOp",EDGE,"E29.3.2.0")}),1.0]])]});
            var Q18;
            Q18=makeQuery(id+"F4.imprint","IMPRINT",FACE,{"disambiguationData":[TD([[makeQuery(id+"F4.imprint","IMPRINT",EDGE,{"derivedFrom":sQuery(id+"F4.wireOp",EDGE,"E29.3.1.0")}),1.0]])]});
            var Q19;
            Q19=makeQuery(id+"F4.imprint","IMPRINT",FACE,{"disambiguationData":[TD([[makeQuery(id+"F4.imprint","IMPRINT",EDGE,{"derivedFrom":sQuery(id+"F4.wireOp",EDGE,"E29.3.0.0")}),1.0]])]});
            extrude(context, id + "F5", {"entities" : qUnion([Q0, Q1, Q2, Q3, Q4, Q5, Q6, Q7, Q8, Q9, Q10, Q11, Q12, Q13, Q14, Q15, Q16, Q17, Q18, Q19]), "operationType" : NewBodyOperationType.ADD, "depth" : 0.8 * mm});
        }
        {
            var Q0;
            Q0=makeQuery(id+"F1.opExtrude","CAP_FACE",FACE,{"disambiguationData":[OSD([sQuery(id+"F0.wireOp",EDGE,"E0.bottom"),sQuery(id+"F0.wireOp",EDGE,"E0.top"),sQuery(id+"F0.wireOp",EDGE,"E0.left"),sQuery(id+"F0.wireOp",EDGE,"E0.right")])],"isStart":false});
            var sketch = newSketch(context, id + "F6", { "sketchPlane" : qUnion([Q0])});
            skCircle(sketch, "E30", {"center": v(48.82, -38.1) * mm, "radius": 0.8 * mm});
            skLineSegment(sketch, "E31.0.0", {"start": v(-50, -40.08) * mm, "end": v(50, -40.08) * mm});
            skLineSegment(sketch, "E31.0.1", {"start": v(50, -40.08) * mm, "end": v(50, 40.08) * mm});
            skLineSegment(sketch, "E31.0.2", {"start": v(50, 40.08) * mm, "end": v(-50, 40.08) * mm});
            skLineSegment(sketch, "E31.0.3", {"start": v(-50, 40.08) * mm, "end": v(-50, -40.08) * mm});
            skCircle(sketch, "E32", {"center": v(48.82, 38.1) * mm, "radius": 0.8 * mm});
            skCircle(sketch, "E33", {"center": v(-48.42, 38.1) * mm, "radius": 0.8 * mm});
            skSolve(sketch);
        }
        {
            var Q0;
            Q0=makeQuery(id+"F6.imprint","IMPRINT",FACE,{"disambiguationData":[TD([[makeQuery(id+"F6.imprint","IMPRINT",EDGE,{"derivedFrom":sQuery(id+"F6.wireOp",EDGE,"E33")}),1.0]])]});
            var Q1;
            Q1=makeQuery(id+"F6.imprint","IMPRINT",FACE,{"disambiguationData":[TD([[makeQuery(id+"F6.imprint","IMPRINT",EDGE,{"derivedFrom":sQuery(id+"F6.wireOp",EDGE,"E32")}),1.0]])]});
            var Q2;
            Q2=makeQuery(id+"F6.imprint","IMPRINT",FACE,{"disambiguationData":[TD([[makeQuery(id+"F6.imprint","IMPRINT",EDGE,{"derivedFrom":sQuery(id+"F6.wireOp",EDGE,"E30")}),1.0]])]});
            extrude(context, id + "F7", {"entities" : qUnion([Q0, Q1, Q2]), "operationType" : NewBodyOperationType.REMOVE, "oppositeDirection" : true, "depth" : 25.4 * mm});
        }
    });
